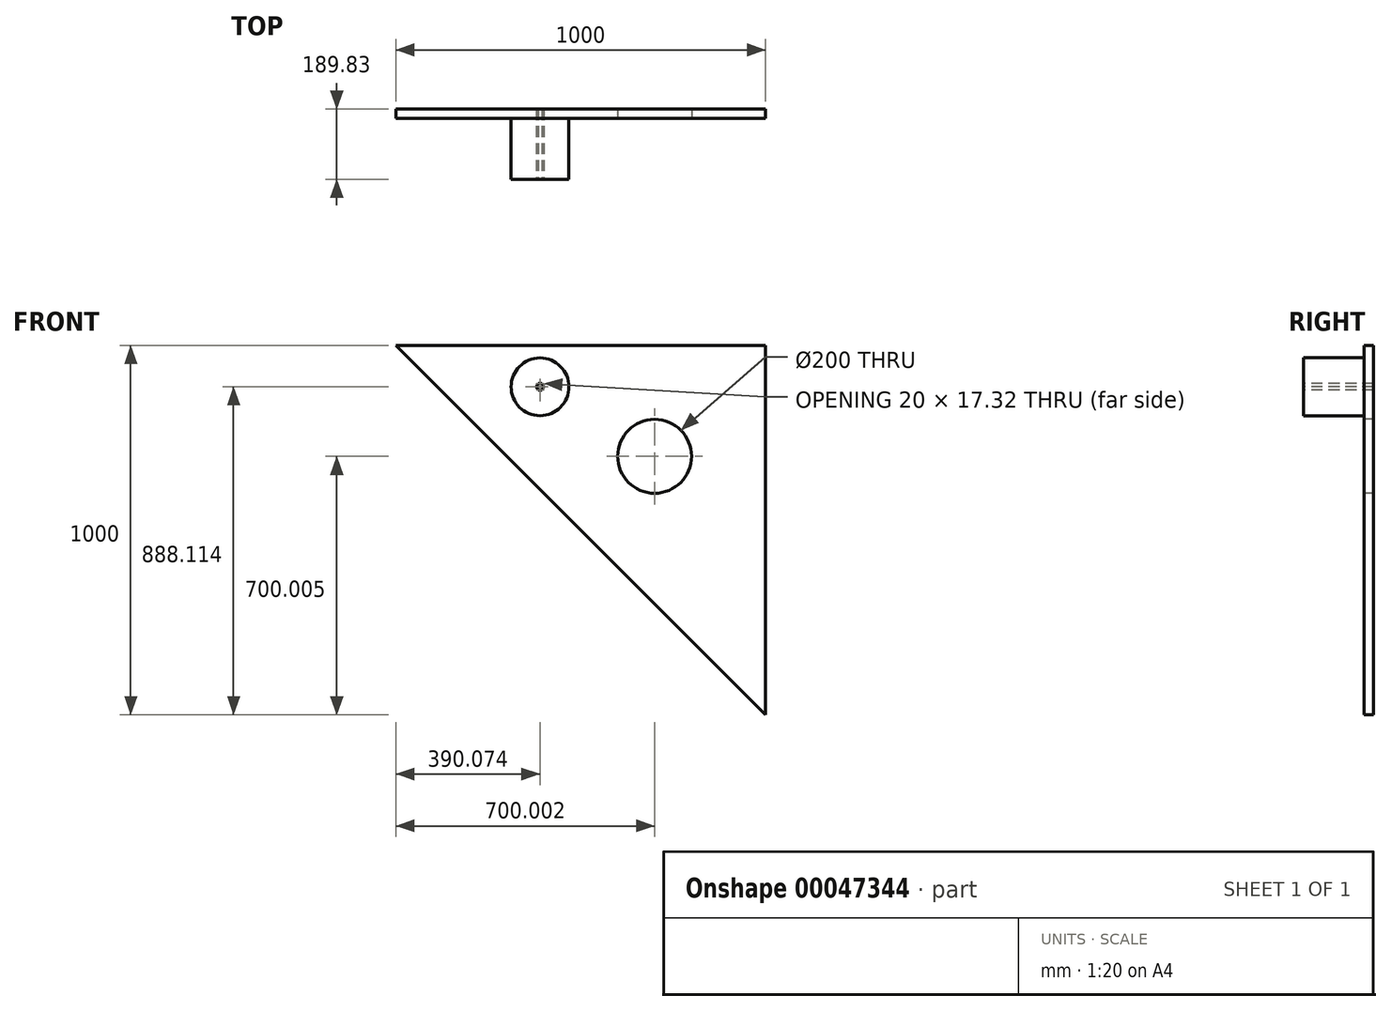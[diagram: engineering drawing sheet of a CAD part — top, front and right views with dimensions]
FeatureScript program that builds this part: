
annotation { "Feature Type Name" : "Feature", "Feature Type Description" : "" }
export const myFeature = defineFeature(function(context is Context, id is Id, definition is map)
    precondition{}
    {
        {
            var Q0;
            Q0=qCreatedBy(makeId("Front.planeOp"),FACE);
            var sketch = newSketch(context, id + "F0", { "sketchPlane" : qUnion([Q0])});
            skLineSegment(sketch, "E0", {"start": v(-9614.97, 1097.85) * mm, "end": v(-8614.97, 1097.85) * mm});
            skLineSegment(sketch, "E1", {"start": v(-8614.97, 1097.85) * mm, "end": v(-8614.97, 97.85) * mm});
            skLineSegment(sketch, "E2", {"start": v(-8614.97, 97.85) * mm, "end": v(-9614.97, 1097.85) * mm});
            skSolve(sketch);
        }
        {
            var Q0;
            Q0 = qSketchRegion(id + "F0", true);
            extrude(context, id + "F1", {"entities" : qUnion([Q0]), "depth" : 25 * mm});
        }
        {
            var Q0;
            Q0=makeQuery(id+"F1.opExtrude","CAP_FACE",FACE,{"disambiguationData":[OSD([sQuery(id+"F0.wireOp",EDGE,"E0"),sQuery(id+"F0.wireOp",EDGE,"E1"),sQuery(id+"F0.wireOp",EDGE,"E2")])],"isStart":false});
            var sketch = newSketch(context, id + "F2", { "sketchPlane" : qUnion([Q0])});
            skCircle(sketch, "E3", {"center": v(-8914.97, 797.85) * mm, "radius": 100 * mm});
            skSolve(sketch);
        }
        {
            var Q0;
            Q0 = qSketchRegion(id + "F2", true);
            extrude(context, id + "F3", {"entities" : qUnion([Q0]), "operationType" : NewBodyOperationType.REMOVE, "endBound" : BoundingType.THROUGH_ALL, "oppositeDirection" : true, "depth" : 25 * mm});
        }
        {
            var Q0;
            Q0=makeQuery(id+"F1.opExtrude","CAP_FACE",FACE,{"disambiguationData":[OSD([sQuery(id+"F0.wireOp",EDGE,"E0"),sQuery(id+"F0.wireOp",EDGE,"E1"),sQuery(id+"F0.wireOp",EDGE,"E2")])],"isStart":false});
            var sketch = newSketch(context, id + "F4", { "sketchPlane" : qUnion([Q0])});
            skCircle(sketch, "E4", {"center": v(-9224.9, 985.96) * mm, "radius": 78.25 * mm});
            skSolve(sketch);
        }
        {
            var Q0;
            Q0 = qSketchRegion(id + "F4", true);
            extrude(context, id + "F5", {"entities" : qUnion([Q0]), "operationType" : NewBodyOperationType.ADD, "depth" : 164.83 * mm});
        }
        {
            var Q0;
            Q0=makeQuery(id+"F5.opExtrude","CAP_FACE",FACE,{"disambiguationData":[OSD([sQuery(id+"F4.wireOp",EDGE,"E4")])],"isStart":false});
            var sketch = newSketch(context, id + "F6", { "sketchPlane" : qUnion([Q0])});
            skCircle(sketch, "E5.cCircle", {"center": v(-9224.9, 985.96) * mm, "radius": 10 * mm, "construction": true});
            skLineSegment(sketch, "E5.0", {"start": v(-9219.9, 977.3) * mm, "end": v(-9229.9, 977.3) * mm});
            skLineSegment(sketch, "E5.1", {"start": v(-9229.9, 977.3) * mm, "end": v(-9234.9, 985.96) * mm});
            skLineSegment(sketch, "E5.2", {"start": v(-9234.9, 985.96) * mm, "end": v(-9229.9, 994.62) * mm});
            skLineSegment(sketch, "E5.3", {"start": v(-9229.9, 994.62) * mm, "end": v(-9219.9, 994.62) * mm});
            skLineSegment(sketch, "E5.4", {"start": v(-9219.9, 994.62) * mm, "end": v(-9214.9, 985.96) * mm});
            skLineSegment(sketch, "E5.5", {"start": v(-9214.9, 985.96) * mm, "end": v(-9219.9, 977.3) * mm});
            skSolve(sketch);
        }
        {
            var Q0;
            Q0 = qSketchRegion(id + "F6", true);
            extrude(context, id + "F7", {"entities" : qUnion([Q0]), "operationType" : NewBodyOperationType.REMOVE, "endBound" : BoundingType.THROUGH_ALL, "oppositeDirection" : true, "depth" : 25 * mm});
        }
    });
